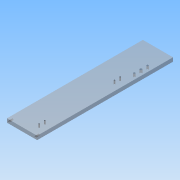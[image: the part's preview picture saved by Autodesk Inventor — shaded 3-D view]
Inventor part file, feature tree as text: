
AUTODESK INVENTOR PART (.ipt)
format: ipt  version: 2016 (Build 200138000, 138)  size: 108,032 bytes
history: native  units: mm
features: sketch x5, hole x4, extrude x1, pattern_linear x1
ambient origin geometry x8: Origin, YZ Plane, XZ Plane, XY Plane, X Axis, Y Axis, Z Axis, Center Point
bodies: Volumenkörper1 (feature_tree)
feature tree (11):
  extrude  "Extrusion1"  Depth=360.0mm
  hole  "Bohrung2"  [1 undecoded]
  hole  "Bohrung4"  [1 undecoded]
  pattern_linear  "Rechteckige Anordnung2"  Count1=3  [1 undecoded]
  hole  "Bohrung5"  [1 undecoded]
  hole  "Bohrung6"  [1 undecoded]
  sketch  "Skizze1"  dims[d0=80.0mm d1=360.0mm]
  sketch  "Skizze2"  dims[d2=10.0mm d3=0.0mm d16=15.0mm]
  sketch  "Skizze4"  dims[d17=70.0mm]
  sketch  "Skizze5"  dims[d18=6.0mm d19=6.0mm d20=4.0mm d21=2.0mm d22=90.0deg d23=8.0mm d24=20.594885mm d34=15.0mm d35=30.0mm]
  sketch  "Skizze6"  dims[d36=55.0mm d37=3.242mm d38=6.0mm d39=4.0mm d40=2.0mm d41=90.0deg d42=8.0mm d43=20.594885mm d44=20.0mm d46=200.0mm d47=5.0mm d48=4.134mm d49=8.0mm d50=4.0mm d51=2.0mm d52=90.0deg d53=10.0mm d54=20.594885mm d55=35.0mm d56=5.0mm d57=6.0mm d58=4.0mm d59=2.0mm d60=90.0deg d61=8.0mm d62=20.594885mm]
note: 5 required parameter values undecoded (feature->parameter linkage not recoverable at this tier; creation-order binding heuristic only, values carry confidence <= 0.55)
